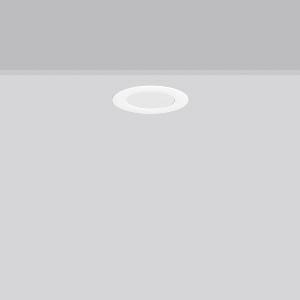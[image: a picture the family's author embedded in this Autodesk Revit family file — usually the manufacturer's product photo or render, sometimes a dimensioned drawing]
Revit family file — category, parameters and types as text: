
# Revit family: toledo_flat_round_e_901451_002_1_bd59
name_source: partatom
category: Lighting Fixtures
units: mm (PartAtom-declared; Revit-internal decimal feet)

## family parameters
Cut with Voids When Loaded = No
Host = Face
Light Source = No
Part Type = Normal
Room Calculation Point = No
Round Connector Dimension = Use Diameter
Shared = No

## types (1)
- TOLEDO FLAT round E (1 x LED Modul 840, 530 lm, 4000)
    Apparent Load = 5 VA
    CIE Flux Codes = 48 79 96 100 100
    Color Rendering = 80
    Color Temperature = 4000
    Default Elevation = 1800 mm
    Description = Series: TOLEDO FLAT round
Ultra thin recessed downlight. Housing: die-cast aluminium. Light guide and diffuser made of non-yellowing PMMA, opal matt. Ceiling installation with spring system. Mounting depth depends on ceiling strength. Including separate LED converter with connecting cable 250 mm. Suitable for through-wiring with separately available accessories. Surface mounted housing as accessory for all sizes. Retrofittable decorative cylinders made of chintz fabric as accessory, optional with satin finish plastic diffuser. Through-wiring box (5 pole) available as accessory. 
Colour: white
Diameter: 148 mm
Height: 2 mm
Cut-out diameter: 128 mm
Recess height: 27-53 mm
Luminaire: recess height: 31-51 mm
Lamp: LED
Socket: without socket
Colour temperature: 4000K
Colour rendering index (CRI): 80
System power: 5 W
Rated luminous flux: 530 lm
Luminous efficiency: 106 lm/W
Control gear: Regulated power supply
Protection class: II
Type of protection: IP 54
    Height = 0 mm  [stored 0 ft]
    Lamp = 1 x LED Modul 840
    Lamp Light Flux = 530 lm
    Lamp count = 1
    Length = 148 mm
    Lifetime = 50000 h
    Luminous efficacy = 106 lm/W
    Manufacturer = RZB
    ModVariant = No
    Model = 901451.002.1
    Mounting Place = Ceiling
    Mounting Type = Recessed
    Number of Poles = 1
    OnlyDefault = Yes
    Power Factor = 1
    Product Name = TOLEDO FLAT round E
    Product group = Recessed downlights
    ProductGroupID = 402
    Protection Class = Protection class II
    Protection Degree = IP 20
    RLX_Detail_Level = 1
    RLX_Emergency_Light_Flux = 0 lm
    RLX_Emergency_Type = 0
    RLX_Emergency_Type_DB = No
    RlxData = <blob elided: 74869 chars, md5=1fb4dd25>
    Socket = socket
    Standby Power = 0 W
    System Light Flux = 530 lm
    System Power = 5 W
    Type Comments = Product without accessories
    Type Image = 901451.002.jpg
    URL = http://relux.com
    VarID = ---
    Voltage = 230 V
    Voltage Range = 220-240 V
    Weight = 0.00 kg
    Width = 0 mm  [stored 0 ft]

note: [stored X ft] marks values corroborated as IEEE doubles in the binary element streams (Revit-internal decimal feet)

## geometry (parser evidence)
native form markers: Blend x4, Sweep x9
no freeform markers — native parametric forms only
